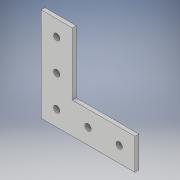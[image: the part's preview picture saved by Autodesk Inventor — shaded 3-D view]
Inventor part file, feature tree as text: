
AUTODESK INVENTOR PART (.ipt)
format: ipt  version: 2018 (Build 220112000, 112)  size: 111,616 bytes
history: native  units: in
note: dims shown in document units (in); Inventor stores cm internally (conversion verified against a paired STEP export)
features: extrude x1, sketch x1
ambient origin geometry x8: Origin, YZ Plane, XZ Plane, XY Plane, X Axis, Y Axis, Z Axis, Center Point
bodies: Solid1 (feature_tree)
feature tree (2):
  extrude  "Extrusion1"  Depth=3.0in
  sketch  "Sketch1"  dims[d0=1.0in d1=3.0in d2=3.0in d3=1.0in d4=0.5in d5=1.0in d6=1.0in d7=1.0in d8=1.0in d9=0.2031in d10=0.125in d11=0.0in]
